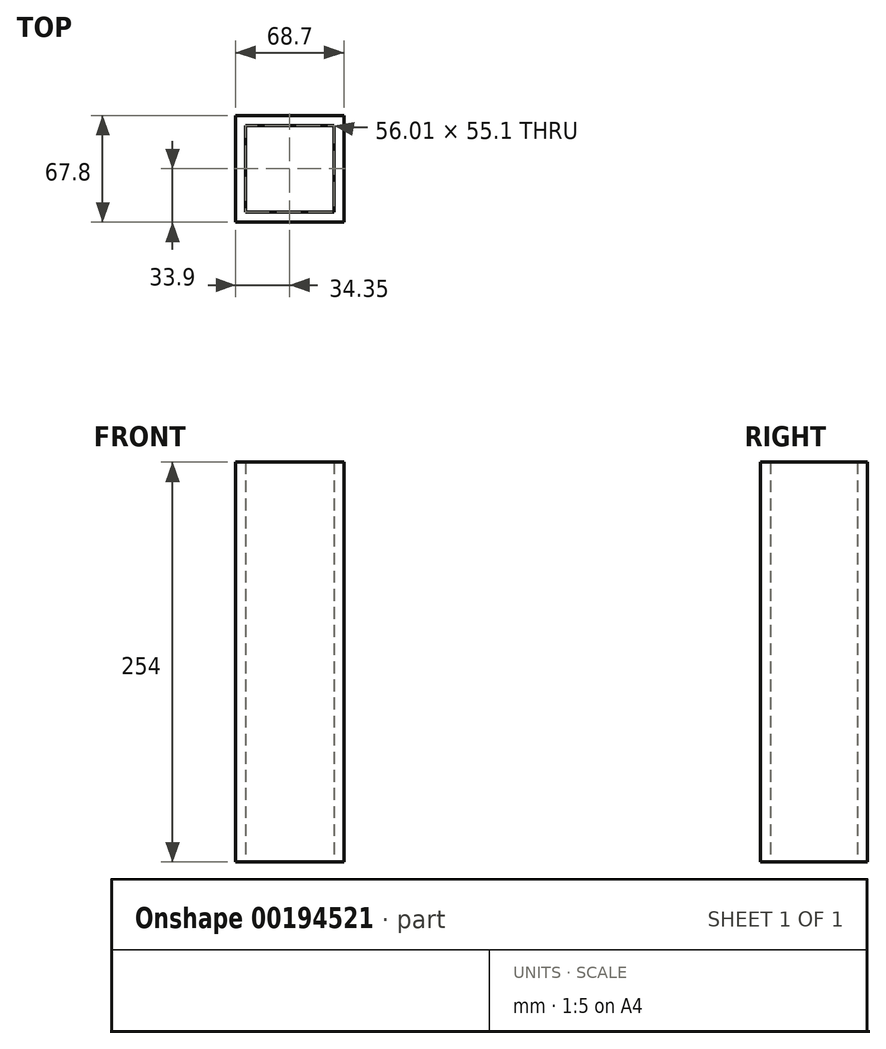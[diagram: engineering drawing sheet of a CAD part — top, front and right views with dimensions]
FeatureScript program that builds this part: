
annotation { "Feature Type Name" : "Feature", "Feature Type Description" : "" }
export const myFeature = defineFeature(function(context is Context, id is Id, definition is map)
    precondition{}
    {
        {
            var Q0;
            Q0=qCreatedBy(makeId("Top.planeOp"),FACE);
            var sketch = newSketch(context, id + "F0", { "sketchPlane" : qUnion([Q0])});
            skLineSegment(sketch, "E0.bottom", {"start": v(28, 27.55) * mm, "end": v(-28, 27.55) * mm});
            skLineSegment(sketch, "E0.top", {"start": v(28, -27.55) * mm, "end": v(-28, -27.55) * mm});
            skLineSegment(sketch, "E0.left", {"start": v(28, 27.55) * mm, "end": v(28, -27.55) * mm});
            skLineSegment(sketch, "E0.right", {"start": v(-28, 27.55) * mm, "end": v(-28, -27.55) * mm});
            skPoint(sketch, "E0.middle", {"position": v(0, 0) * mm});
            skLineSegment(sketch, "E1.0", {"start": v(-34.35, 33.9) * mm, "end": v(-34.35, -33.9) * mm});
            skLineSegment(sketch, "E1.1", {"start": v(34.35, 33.9) * mm, "end": v(-34.35, 33.9) * mm});
            skLineSegment(sketch, "E1.2", {"start": v(34.35, 33.9) * mm, "end": v(34.35, -33.9) * mm});
            skLineSegment(sketch, "E1.3", {"start": v(34.35, -33.9) * mm, "end": v(-34.35, -33.9) * mm});
            skSolve(sketch);
        }
        {
            var Q0;
            Q0=makeQuery(id+"F0.imprint","IMPRINT",FACE,{"disambiguationData":[TD([[makeQuery(id+"F0.imprint","IMPRINT",EDGE,{"derivedFrom":sQuery(id+"F0.wireOp",EDGE,"E0.bottom")}),-1.0]])]});
            extrude(context, id + "F1", {"entities" : qUnion([Q0]), "depth" : 254 * mm});
        }
    });
